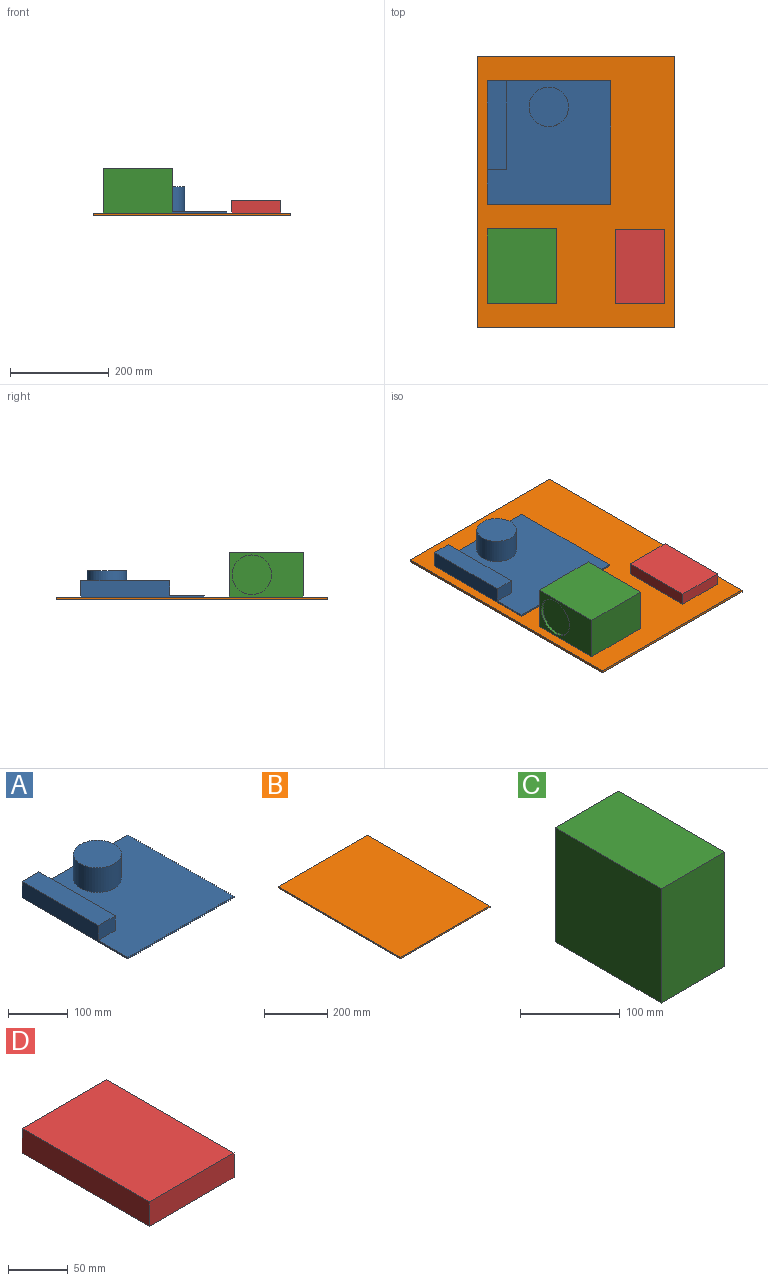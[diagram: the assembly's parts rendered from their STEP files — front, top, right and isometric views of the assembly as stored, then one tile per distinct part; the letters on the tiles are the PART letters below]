
ASSEMBLY  parts=4 mates=3
PART A: 11 faces, bbox 250x250x53 mm
  f0: plane 250x250mm, normal (0,0,1), area 50273.5mm2, adj f1,f2,f3,f4,f6,f8,f9
  f1: plane 250x33mm, normal (0,1,0), area 1950mm2, adj f0,f2,f4,f5,f9,f10
  f2: plane 250x33mm, normal (-1,0,0), area 6150mm2, adj f0,f1,f3,f5,f8,f10
  f3: plane 250x3mm, normal (0,-1,0), area 750mm2, adj f0,f2,f4,f5
  f4: plane 250x3mm, normal (1,0,0), area 750mm2, adj f0,f1,f3,f5
  f5: plane 250x250mm, normal (0,0,-1), area 62500mm2, adj f1,f2,f3,f4
  f6: cylinder r=40mm len=80mm, axis (0,0,-1), area 12566.4mm2, adj f0,f7
  f7: plane 80x80mm, normal (0,0,1), area 5026.5mm2, adj f6
  f8: plane 40x30mm, normal (0,-1,0), area 1200mm2, adj f0,f2,f9,f10
  f9: plane 180x30mm, normal (1,0,0), area 5400mm2, adj f0,f1,f8,f10
  f10: plane 180x40mm, normal (0,0,1), area 7200mm2, adj f1,f2,f8,f9
PART B: 6 faces, bbox 400x550x5 mm
  f0: plane 400x5mm, normal (0,1,0), area 2000mm2, adj f1,f3,f4,f5
  f1: plane 550x5mm, normal (-1,0,0), area 2750mm2, adj f0,f2,f4,f5
  f2: plane 400x5mm, normal (0,-1,0), area 2000mm2, adj f1,f3,f4,f5
  f3: plane 550x5mm, normal (1,0,0), area 2750mm2, adj f0,f2,f4,f5
  f4: plane 550x400mm, normal (0,0,1), area 220000mm2, adj f0,f1,f2,f3
  f5: plane 550x400mm, normal (0,0,-1), area 220000mm2, adj f0,f1,f2,f3
PART C: 8 faces, bbox 90x150x140 mm
  f0: plane 140x90mm, normal (0,1,0), area 12600mm2, adj f1,f3,f4,f5
  f1: plane 150x140mm, normal (-1,0,0), area 21000mm2, adj f0,f2,f4,f5
  f2: plane 140x90mm, normal (0,-1,0), area 12600mm2, adj f1,f3,f4,f5
  f3: plane 150x140mm, normal (1,0,0), area 21000mm2, adj f0,f2,f4,f5
  f4: plane 150x90mm, normal (0,0,1), area 13500mm2, adj f0,f1,f2,f3
  f5: plane 150x90mm, normal (0,0,-1), area 8473.5mm2, adj f0,f1,f2,f3,f6
  f6: cylinder r=40mm len=80mm, axis (0,0,-1), area 1256.6mm2, adj f5,f7
  f7: plane 80x80mm, normal (0,0,-1), area 5026.5mm2, adj f6
PART D: 6 faces, bbox 100x150x25 mm
  f0: plane 100x25mm, normal (0,1,0), area 2500mm2, adj f1,f3,f4,f5
  f1: plane 150x25mm, normal (-1,0,0), area 3750mm2, adj f0,f2,f4,f5
  f2: plane 100x25mm, normal (0,-1,0), area 2500mm2, adj f1,f3,f4,f5
  f3: plane 150x25mm, normal (1,0,0), area 3750mm2, adj f0,f2,f4,f5
  f4: plane 150x100mm, normal (0,0,1), area 15000mm2, adj f0,f1,f2,f3
  f5: plane 150x100mm, normal (0,0,-1), area 15000mm2, adj f0,f1,f2,f3
PLACE A t=(-55,100,5)mm
PLACE B at identity fixed
PLACE C rot(axis=(0,1,0),90deg) t=(-180,-150,50)mm
PLACE D t=(130,-150,5)mm
MATE fastened A.f5 <-> B.f4  axis (0,0,-1) through (-180,225,5)mm
MATE fastened C.f3 <-> B.f4  axis (0,0,-1) through (-180,-225,5)mm
MATE fastened D.f5 <-> B.f4  axis (0,0,-1) through (180,-225,5)mm
